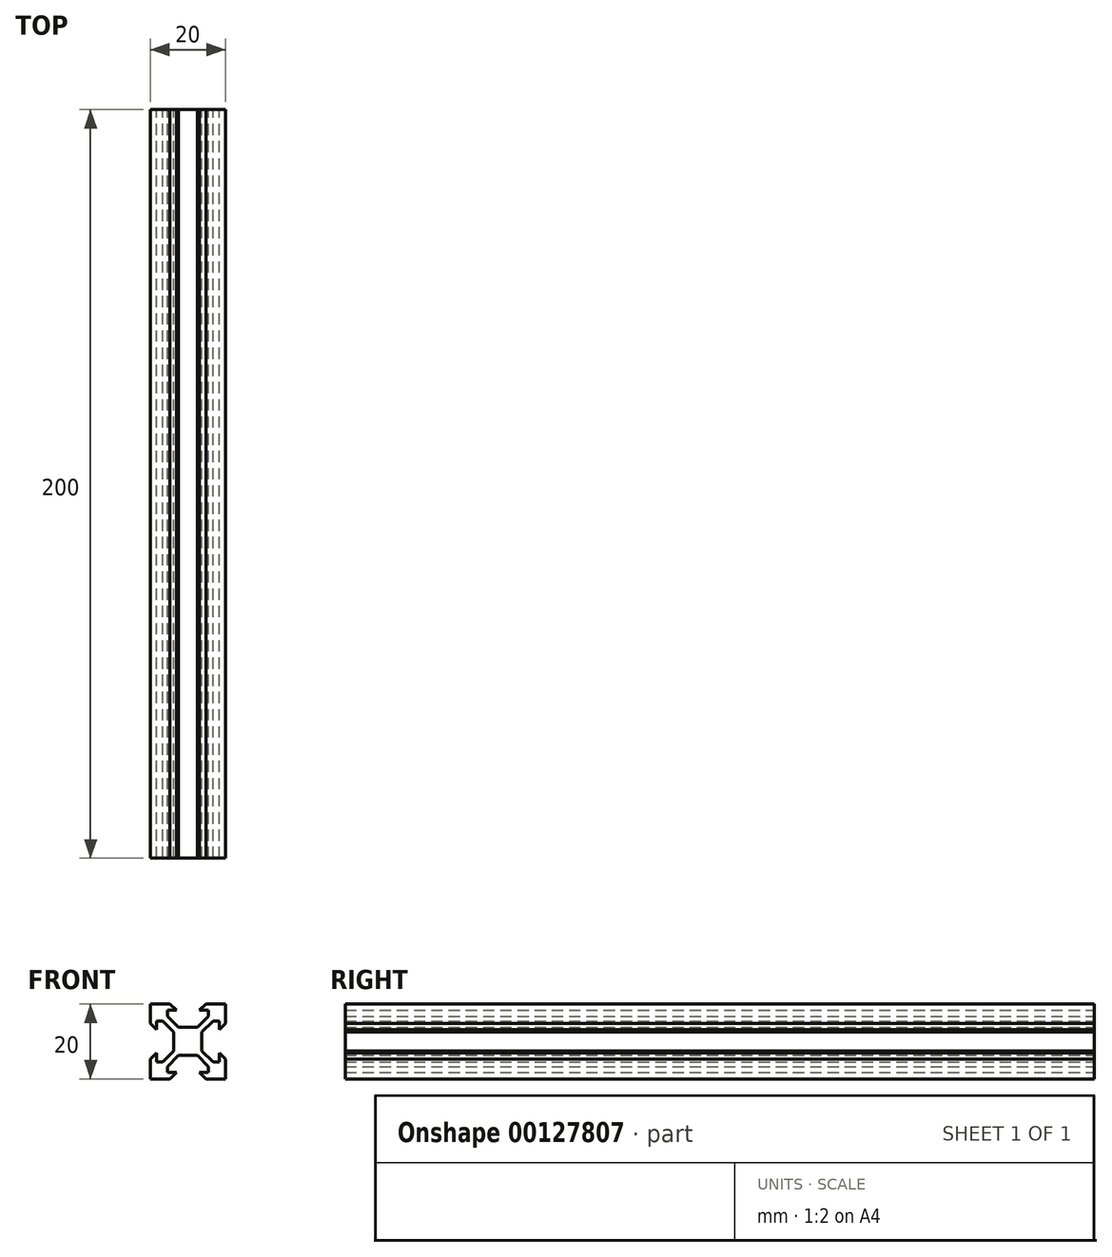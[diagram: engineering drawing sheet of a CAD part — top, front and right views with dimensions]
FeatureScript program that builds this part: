
annotation { "Feature Type Name" : "Feature", "Feature Type Description" : "" }
export const myFeature = defineFeature(function(context is Context, id is Id, definition is map)
    precondition{}
    {
        {
            var Q0;
            Q0=qCreatedBy(makeId("Front.planeOp"),FACE);
            var sketch = newSketch(context, id + "F0", { "sketchPlane" : qUnion([Q0])});
            skLineSegment(sketch, "E0", {"start": v(-10, 10) * mm, "end": v(-4.78, 10) * mm});
            skLineSegment(sketch, "E1", {"start": v(-4.78, 10) * mm, "end": v(-3.1, 8.33) * mm});
            skLineSegment(sketch, "E2", {"start": v(-3.1, 8.32) * mm, "end": v(-5.5, 8.32) * mm});
            skLineSegment(sketch, "E3", {"start": v(-5.5, 8.32) * mm, "end": v(-5.5, 6.68) * mm});
            skLineSegment(sketch, "E4", {"start": v(-5.5, 6.68) * mm, "end": v(-2.57, 3.75) * mm});
            skLineSegment(sketch, "E5", {"start": v(-2.57, 3.75) * mm, "end": v(0, 3.75) * mm});
            skLineSegment(sketch, "E6", {"start": v(0, 0) * mm, "end": v(0, -2.66) * mm, "construction": true});
            skLineSegment(sketch, "E7", {"start": v(0, 0) * mm, "end": v(-3.75, 0) * mm, "construction": true});
            skLineSegment(sketch, "E8", {"start": v(-10, 10) * mm, "end": v(-10, 4.77) * mm});
            skLineSegment(sketch, "E9", {"start": v(-10, 4.78) * mm, "end": v(-8.33, 3.1) * mm});
            skLineSegment(sketch, "E10", {"start": v(-8.32, 3.1) * mm, "end": v(-8.32, 5.5) * mm});
            skLineSegment(sketch, "E11", {"start": v(-8.33, 5.5) * mm, "end": v(-6.68, 5.5) * mm});
            skLineSegment(sketch, "E12", {"start": v(-6.68, 5.5) * mm, "end": v(-3.75, 2.57) * mm});
            skLineSegment(sketch, "E13", {"start": v(-3.75, 2.57) * mm, "end": v(-3.75, 0) * mm});
            skCircle(sketch, "E14", {"center": v(0, 0) * mm, "radius": 2.1 * mm, "construction": true});
            skLineSegment(sketch, "E15.1.0", {"start": v(-5.5, -6.68) * mm, "end": v(-2.57, -3.75) * mm});
            skLineSegment(sketch, "E15.1.1", {"start": v(-5.5, -8.33) * mm, "end": v(-5.5, -6.68) * mm});
            skLineSegment(sketch, "E15.1.2", {"start": v(-3.1, -8.32) * mm, "end": v(-5.5, -8.32) * mm});
            skLineSegment(sketch, "E15.1.3", {"start": v(-4.78, -10) * mm, "end": v(-3.1, -8.33) * mm});
            skLineSegment(sketch, "E15.1.4", {"start": v(-10, -10) * mm, "end": v(-4.77, -10) * mm});
            skLineSegment(sketch, "E15.1.5", {"start": v(-8.32, -5.5) * mm, "end": v(-6.68, -5.5) * mm});
            skLineSegment(sketch, "E15.1.6", {"start": v(-8.32, -3.1) * mm, "end": v(-8.32, -5.5) * mm});
            skLineSegment(sketch, "E15.1.7", {"start": v(-10, -4.77) * mm, "end": v(-8.33, -3.1) * mm});
            skLineSegment(sketch, "E15.1.8", {"start": v(-10, -10) * mm, "end": v(-10, -4.77) * mm});
            skLineSegment(sketch, "E15.1.9", {"start": v(-2.57, -3.75) * mm, "end": v(0, -3.75) * mm});
            skLineSegment(sketch, "E15.1.10", {"start": v(-6.68, -5.5) * mm, "end": v(-3.75, -2.57) * mm});
            skLineSegment(sketch, "E15.1.11", {"start": v(-3.75, -2.57) * mm, "end": v(-3.75, 0) * mm});
            skLineSegment(sketch, "E15.2.0", {"start": v(6.68, -5.5) * mm, "end": v(3.75, -2.57) * mm});
            skLineSegment(sketch, "E15.2.1", {"start": v(8.33, -5.5) * mm, "end": v(6.68, -5.5) * mm});
            skLineSegment(sketch, "E15.2.2", {"start": v(8.32, -3.1) * mm, "end": v(8.32, -5.5) * mm});
            skLineSegment(sketch, "E15.2.3", {"start": v(10, -4.78) * mm, "end": v(8.33, -3.1) * mm});
            skLineSegment(sketch, "E15.2.4", {"start": v(10, -10) * mm, "end": v(10, -4.78) * mm});
            skLineSegment(sketch, "E15.2.5", {"start": v(5.5, -8.32) * mm, "end": v(5.5, -6.68) * mm});
            skLineSegment(sketch, "E15.2.6", {"start": v(3.1, -8.32) * mm, "end": v(5.5, -8.32) * mm});
            skLineSegment(sketch, "E15.2.7", {"start": v(4.77, -10) * mm, "end": v(3.1, -8.33) * mm});
            skLineSegment(sketch, "E15.2.8", {"start": v(10, -10) * mm, "end": v(4.77, -10) * mm});
            skLineSegment(sketch, "E15.2.9", {"start": v(3.75, -2.57) * mm, "end": v(3.75, 0) * mm});
            skLineSegment(sketch, "E15.2.10", {"start": v(5.5, -6.68) * mm, "end": v(2.57, -3.75) * mm});
            skLineSegment(sketch, "E15.2.11", {"start": v(2.57, -3.75) * mm, "end": v(0, -3.75) * mm});
            skLineSegment(sketch, "E15.3.0", {"start": v(5.5, 6.68) * mm, "end": v(2.57, 3.75) * mm});
            skLineSegment(sketch, "E15.3.1", {"start": v(5.5, 8.33) * mm, "end": v(5.5, 6.68) * mm});
            skLineSegment(sketch, "E15.3.2", {"start": v(3.1, 8.32) * mm, "end": v(5.5, 8.32) * mm});
            skLineSegment(sketch, "E15.3.3", {"start": v(4.78, 10) * mm, "end": v(3.1, 8.33) * mm});
            skLineSegment(sketch, "E15.3.4", {"start": v(10, 10) * mm, "end": v(4.78, 10) * mm});
            skLineSegment(sketch, "E15.3.5", {"start": v(8.32, 5.5) * mm, "end": v(6.68, 5.5) * mm});
            skLineSegment(sketch, "E15.3.6", {"start": v(8.32, 3.1) * mm, "end": v(8.32, 5.5) * mm});
            skLineSegment(sketch, "E15.3.7", {"start": v(10, 4.77) * mm, "end": v(8.33, 3.1) * mm});
            skLineSegment(sketch, "E15.3.8", {"start": v(10, 10) * mm, "end": v(10, 4.77) * mm});
            skLineSegment(sketch, "E15.3.9", {"start": v(2.57, 3.75) * mm, "end": v(0, 3.75) * mm});
            skLineSegment(sketch, "E15.3.10", {"start": v(6.68, 5.5) * mm, "end": v(3.75, 2.57) * mm});
            skLineSegment(sketch, "E15.3.11", {"start": v(3.75, 2.57) * mm, "end": v(3.75, 0) * mm});
            skSolve(sketch);
        }
        {
            var Q0;
            Q0=qSketchRegion(id+"F0",true);
            extrude(context, id + "F1", {"entities" : qUnion([Q0]), "endBound" : BoundingType.SYMMETRIC, "depth" : 200 * mm});
        }
    });
